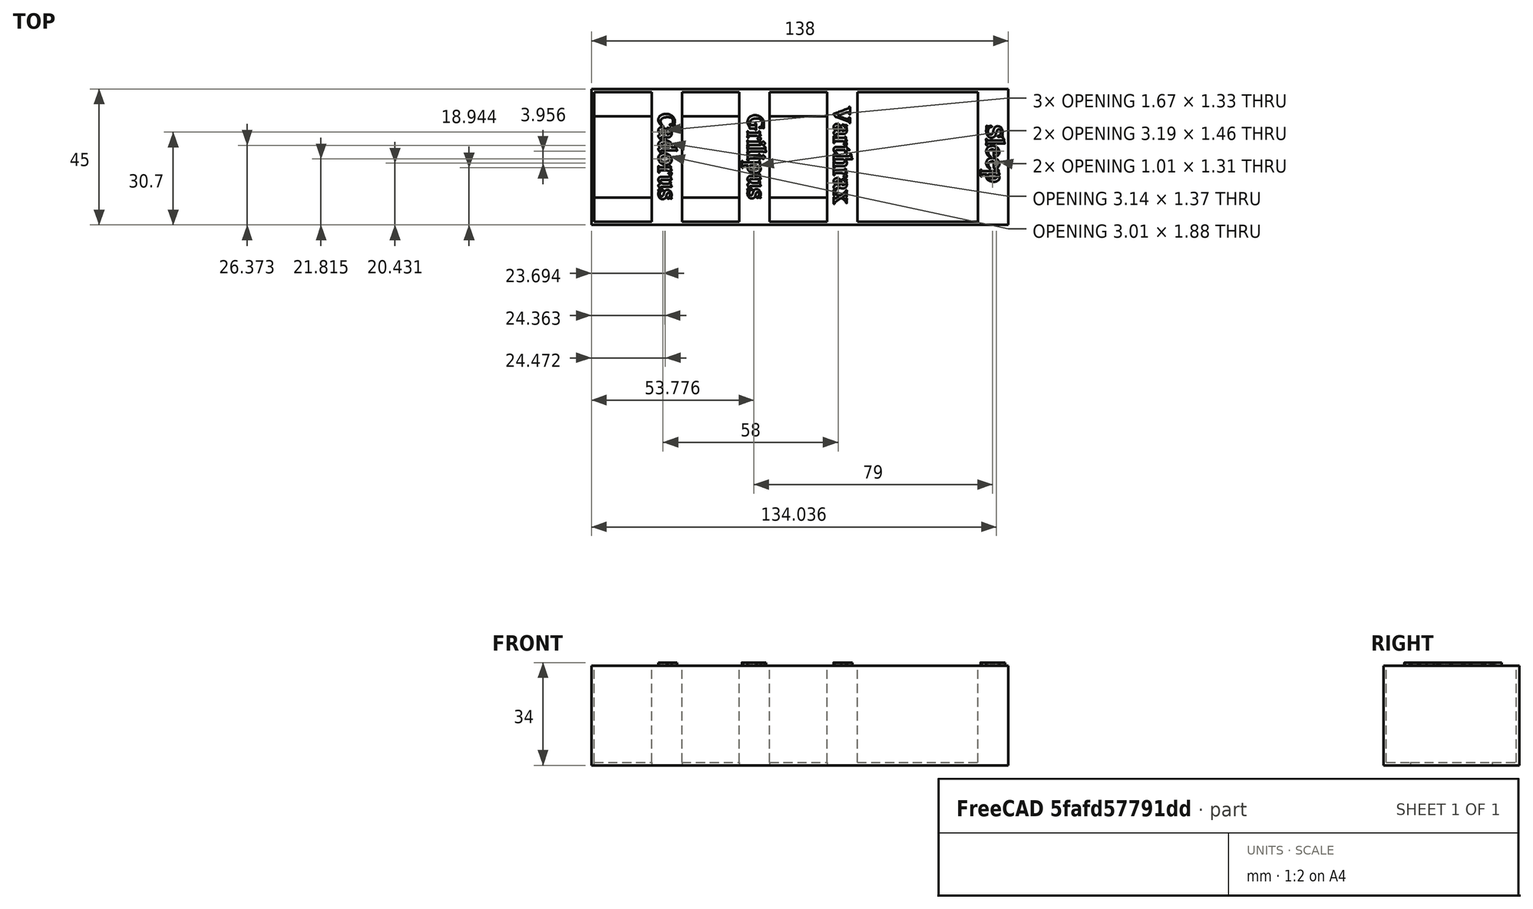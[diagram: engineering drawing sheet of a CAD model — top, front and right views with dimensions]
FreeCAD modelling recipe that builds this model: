
FCSTD DOCUMENT  (FreeCAD 0.18R4 (GitTag))
Label: dragons
License: All rights reserved
LicenseURL: http://en.wikipedia.org/wiki/All_rights_reserved
objects: Part::Box×11, Part::MultiFuse×4, Part::Part2DObjectPython×4, Part::Extrusion×4, Part::Cut×2
note: 25 computed .brp shape members not serialized (recipe doc carries the construction recipe); baked Part::Feature solids carry a one-line shape summary decoded from their .brp

FEATURE [Part::Box] Box  label="Cube"
  AttacherType = Attacher::AttachEngine3D
  Height = 33
  Length = 202
  Placement = pos=(0,-1,0) rot=(0,0,1;0rad)
  Width = 45
FEATURE [Part::Box] Box001  label="Cube001"
  AttacherType = Attacher::AttachEngine3D
  Height = 33
  Length = 200
  Placement = pos=(1,0,0) rot=(0,0,1;0rad)
  Width = 43
FEATURE [Part::Cut] Cut
  Base = -> Box
  Tool = -> Box001
FEATURE [Part::Box] Box002  label="Cube002"
  AttacherType = Attacher::AttachEngine3D
  Height = 1
  Length = 202
  Width = 8
FEATURE [Part::Box] Box003  label="Cube003"
  AttacherType = Attacher::AttachEngine3D
  Height = 1
  Length = 202
  Placement = pos=(0,35,0) rot=(0,0,1;0rad)
  Width = 8
FEATURE [Part::MultiFuse] Fusion
  Shapes = -> [Cut,Box002,Box003]
FEATURE [Part::Box] Box004  label="Cube004"
  AttacherType = Attacher::AttachEngine3D
  Height = 33
  Length = 10
  Placement = pos=(20,0,0) rot=(0,0,1;0rad)
  Width = 43
FEATURE [Part::Box] Box005  label="Cube005"
  AttacherType = Attacher::AttachEngine3D
  Height = 33
  Length = 10
  Placement = pos=(49,0,0) rot=(0,0,1;0rad)
  Width = 43
FEATURE [Part::Box] Box006  label="Cube006"
  AttacherType = Attacher::AttachEngine3D
  Height = 33
  Length = 10
  Placement = pos=(78,0,0) rot=(0,0,1;0rad)
  Width = 43
FEATURE [Part::Box] Box007  label="Cube007"
  AttacherType = Attacher::AttachEngine3D
  Height = 33
  Length = 10
  Placement = pos=(128,0,0) rot=(0,0,1;0rad)
  Width = 43
FEATURE [Part::Box] Box008  label="Cube008"
  AttacherType = Attacher::AttachEngine3D
  Height = 33
  Length = 10
  Placement = pos=(168,0,0) rot=(0,0,1;0rad)
  Width = 43
FEATURE [Part::Box] Box009  label="Cube009"
  AttacherType = Attacher::AttachEngine3D
  Height = 33
  Length = 68
  Placement = pos=(138,-1,0) rot=(0,0,1;0rad)
  Width = 45
FEATURE [Part::MultiFuse] Fusion001
  Shapes = -> [Fusion,Box004,Box006,Box005,Box008,Box007]
FEATURE [Part::Box] Box010  label="Cube010"
  AttacherType = Attacher::AttachEngine3D
  Height = 1
  Length = 43
  Placement = pos=(88,0,0) rot=(0,0,1;0rad)
  Width = 43
FEATURE [Part::Part2DObjectPython] ShapeString  # Draft 2D object (typed FeaturePython)
  FontFile = <userpath>/Downloads/talisman/Caxton Bold.otf
  Placement = pos=(81.94,33.31,33) rot=(0,0,1;0rad)
  Size = 3
  String = Cadorus
  Tracking = 0
FEATURE [Part::Part2DObjectPython] ShapeString001  # Draft 2D object (typed FeaturePython)
  FontFile = <userpath>/Downloads/talisman/Caxton Bold.otf
  Placement = pos=(81.94,33.31,33) rot=(0,0,1;0rad)
  Size = 3
  String = Grilipus
  Tracking = 0
FEATURE [Part::Part2DObjectPython] ShapeString002  # Draft 2D object (typed FeaturePython)
  FontFile = <userpath>/Downloads/talisman/Caxton Bold.otf
  Placement = pos=(81.94,33.31,33) rot=(0,0,1;0rad)
  Size = 3
  String = Varthrax
  Tracking = 0
FEATURE [Part::Part2DObjectPython] ShapeString003  # Draft 2D object (typed FeaturePython)
  FontFile = <userpath>/Downloads/talisman/Caxton Bold.otf
  Placement = pos=(81.94,33.31,33) rot=(0,0,1;0rad)
  Size = 3
  String = Sleep
  Tracking = 0
FEATURE [Part::Extrusion] Extrude
  Base = -> ShapeString
  Dir = (0,0,1)
  DirMode = 2
  FaceMakerClass = Part::FaceMakerBullseye
  LengthFwd = 1
  LengthRev = 0
  Placement = pos=(-11,118,0) rot=(0,0,-1;1.5708rad)
  Solid = false
  Symmetric = false
FEATURE [Part::Extrusion] Extrude001
  Base = -> ShapeString001
  Dir = (0,0,1)
  DirMode = 2
  FaceMakerClass = Part::FaceMakerBullseye
  LengthFwd = 1
  LengthRev = 0
  Placement = pos=(18.5,117.5,0) rot=(0,0,-1;1.5708rad)
  Solid = false
  Symmetric = false
FEATURE [Part::Extrusion] Extrude002
  Base = -> ShapeString002
  Dir = (0,0,1)
  DirMode = 2
  FaceMakerClass = Part::FaceMakerBullseye
  LengthFwd = 1
  LengthRev = 0
  Placement = pos=(47,120,0) rot=(0,0,-1;1.5708rad)
  Solid = false
  Symmetric = false
FEATURE [Part::Extrusion] Extrude003
  Base = -> ShapeString003
  Dir = (0,0,1)
  DirMode = 2
  FaceMakerClass = Part::FaceMakerBullseye
  LengthFwd = 1
  LengthRev = 0
  Placement = pos=(97.5,114,0) rot=(0,0,-1;1.5708rad)
  Solid = false
  Symmetric = false
FEATURE [Part::MultiFuse] Fusion004
  Shapes = -> [Extrude002,Extrude,Extrude001,Extrude003]
FEATURE [Part::Cut] Cut001
  Base = -> Fusion001
  Tool = -> Box009
FEATURE [Part::MultiFuse] Fusion005
  Shapes = -> [Box010,Cut001]
